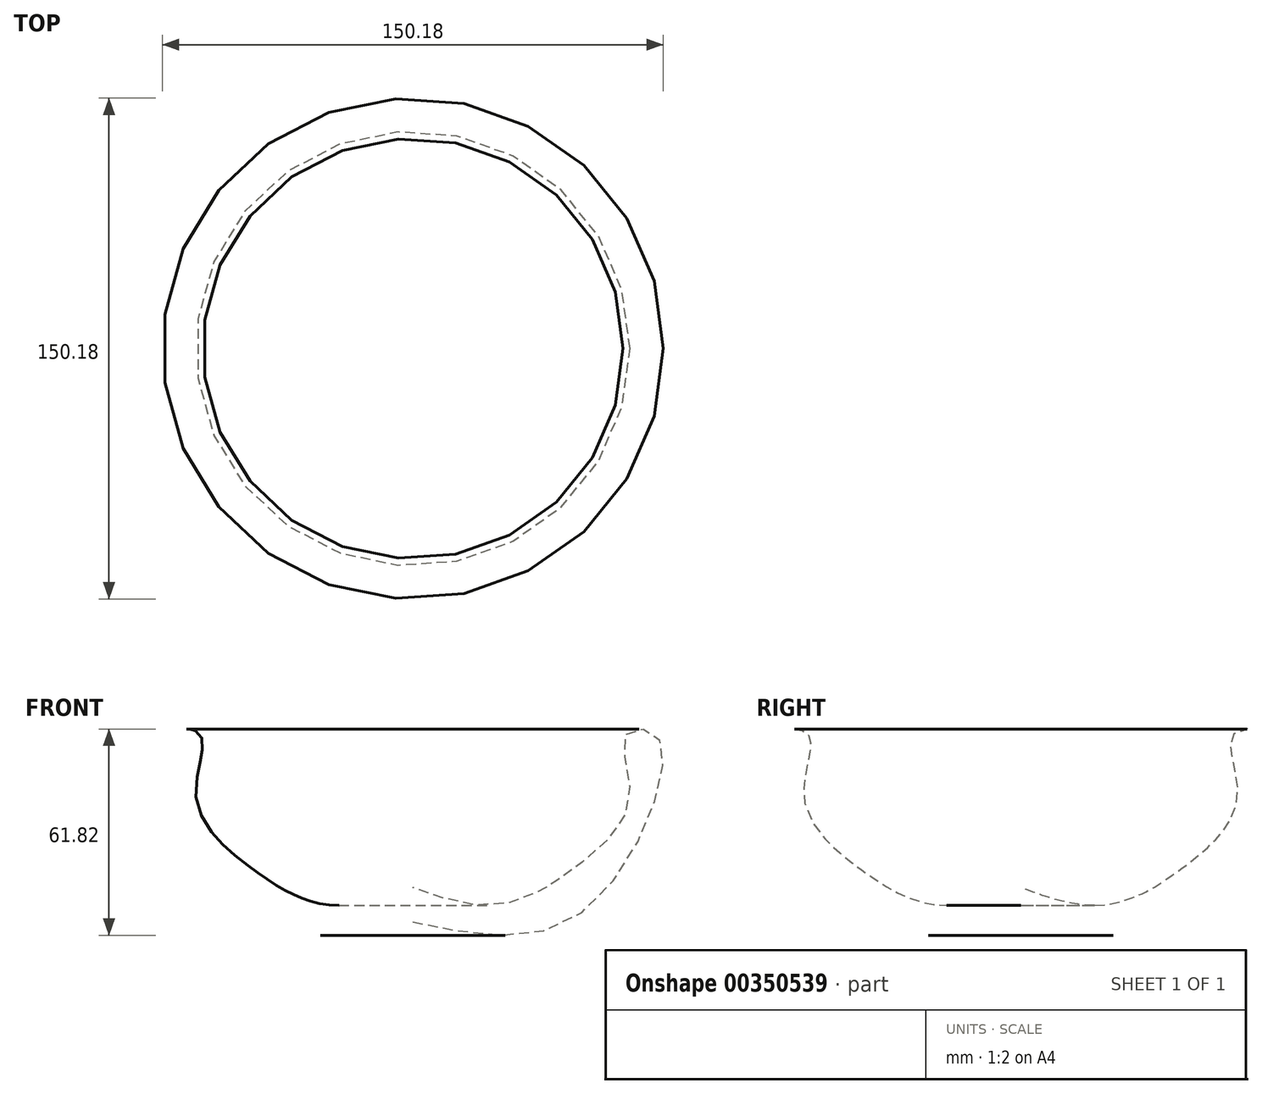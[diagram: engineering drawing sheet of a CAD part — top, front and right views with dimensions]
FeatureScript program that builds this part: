
annotation { "Feature Type Name" : "Feature", "Feature Type Description" : "" }
export const myFeature = defineFeature(function(context is Context, id is Id, definition is map)
    precondition{}
    {
        {
            var Q0;
            Q0=qCreatedBy(makeId("Front.planeOp"),FACE);
            var sketch = newSketch(context, id + "F0", { "sketchPlane" : qUnion([Q0])});
            skLineSegment(sketch, "E0", {"start": v(0, 0) * mm, "end": v(0, 10.33) * mm});
            skFitSpline(sketch, "E1", {"points": [v(0, 0) * mm, v(46.13, 0) * mm, v(73.33, 38.9) * mm, v(72.3, 56.46) * mm, v(63.7, 56.12) * mm, v(65.07, 38.9) * mm, v(53.36, 19.97) * mm, v(39.72, 10.2) * mm, v(39.66, 10.17) * mm, v(39.39, 10.03) * mm, v(25.82, 5.16) * mm, v(0, 10.33) * mm], "startDerivative": vector(294.37, -63.25) * mm, "endDerivative": vector(-200.45, 75.7) * mm});
            skSolve(sketch);
        }
        {
            var Q0;
            Q0=makeQuery(id+"F0.imprint","IMPRINT",FACE,{"disambiguationData":[TD([[makeQuery(id+"F0.imprint","IMPRINT",EDGE,{"derivedFrom":sQuery(id+"F0.wireOp",EDGE,"E0")}),-1.0]])]});
            var Q1;
            Q1=sQuery(id+"F0.wireOp",EDGE,"E0");
            revolve(context, id + "F1", {"entities" : qUnion([Q0]), "axis" : qUnion([Q1]), "revolveType" : RevolveType.FULL});
        }
    });
